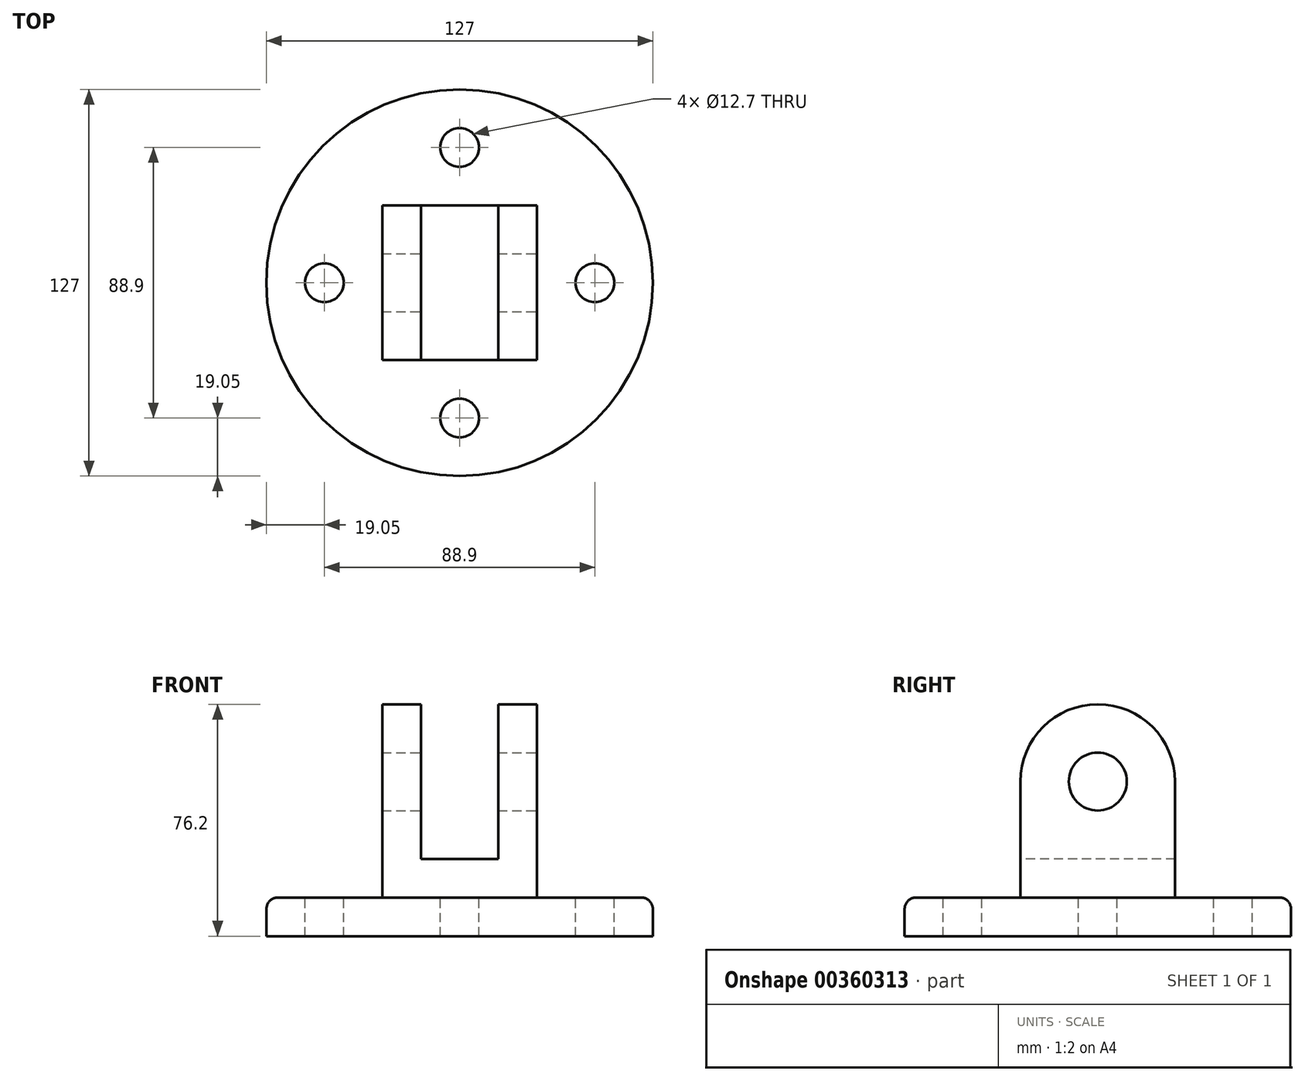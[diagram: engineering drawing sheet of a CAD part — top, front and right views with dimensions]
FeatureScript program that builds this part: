
annotation { "Feature Type Name" : "Feature", "Feature Type Description" : "" }
export const myFeature = defineFeature(function(context is Context, id is Id, definition is map)
    precondition{}
    {
        {
            var Q0;
            Q0=qCreatedBy(makeId("Top.planeOp"),FACE);
            var sketch = newSketch(context, id + "F0", { "sketchPlane" : qUnion([Q0])});
            skCircle(sketch, "E0", {"center": v(0, 0) * mm, "radius": 63.5 * mm});
            skSolve(sketch);
        }
        {
            var Q0;
            Q0 = qSketchRegion(id + "F0", true);
            extrude(context, id + "F1", {"entities" : qUnion([Q0]), "depth" : 12.7 * mm});
        }
        {
            var Q0;
            Q0=makeQuery(id+"F1.opExtrude","CAP_FACE",FACE,{"disambiguationData":[OSD([sQuery(id+"F0.wireOp",EDGE,"E0")])],"isStart":false});
            var sketch = newSketch(context, id + "F2", { "sketchPlane" : qUnion([Q0])});
            skLineSegment(sketch, "E1.bottom", {"start": v(25.4, 25.4) * mm, "end": v(-25.4, 25.4) * mm});
            skLineSegment(sketch, "E1.top", {"start": v(25.4, -25.4) * mm, "end": v(-25.4, -25.4) * mm});
            skLineSegment(sketch, "E1.left", {"start": v(25.4, 25.4) * mm, "end": v(25.4, -25.4) * mm});
            skLineSegment(sketch, "E1.right", {"start": v(-25.4, 25.4) * mm, "end": v(-25.4, -25.4) * mm});
            skPoint(sketch, "E1.middle", {"position": v(0, 0) * mm});
            skSolve(sketch);
        }
        {
            var Q0;
            Q0 = qSketchRegion(id + "F2", true);
            extrude(context, id + "F3", {"entities" : qUnion([Q0]), "operationType" : NewBodyOperationType.ADD, "depth" : 12.7 * mm});
        }
        {
            var Q0;
            Q0=makeQuery(id+"F3.opExtrude","CAP_FACE",FACE,{"disambiguationData":[OSD([sQuery(id+"F2.wireOp",EDGE,"E1.bottom"),sQuery(id+"F2.wireOp",EDGE,"E1.top"),sQuery(id+"F2.wireOp",EDGE,"E1.left"),sQuery(id+"F2.wireOp",EDGE,"E1.right")])],"isStart":false});
            var sketch = newSketch(context, id + "F4", { "sketchPlane" : qUnion([Q0])});
            skLineSegment(sketch, "E2.bottom", {"start": v(-10.67, -25.4) * mm, "end": v(-25.4, -25.4) * mm});
            skLineSegment(sketch, "E2.top", {"start": v(-10.67, 25.4) * mm, "end": v(-25.4, 25.4) * mm});
            skLineSegment(sketch, "E2.left", {"start": v(-10.67, -25.4) * mm, "end": v(-10.67, 25.4) * mm});
            skLineSegment(sketch, "E2.right", {"start": v(-25.4, -25.4) * mm, "end": v(-25.4, 25.4) * mm});
            skLineSegment(sketch, "E3.bottom", {"start": v(25.4, -25.4) * mm, "end": v(12.7, -25.4) * mm});
            skLineSegment(sketch, "E3.top", {"start": v(25.4, 25.4) * mm, "end": v(12.7, 25.4) * mm});
            skLineSegment(sketch, "E3.left", {"start": v(25.4, -25.4) * mm, "end": v(25.4, 25.4) * mm});
            skLineSegment(sketch, "E3.right", {"start": v(12.7, -25.4) * mm, "end": v(12.7, 25.4) * mm});
            skSolve(sketch);
        }
        {
            var Q0;
            Q0 = qSketchRegion(id + "F4", true);
            extrude(context, id + "F5", {"entities" : qUnion([Q0]), "operationType" : NewBodyOperationType.ADD, "depth" : 25.4 * mm});
        }
        {
            var Q0;
            Q0=qCreatedBy(makeId("Right.planeOp"),FACE);
            var sketch = newSketch(context, id + "F6", { "sketchPlane" : qUnion([Q0])});
            skArc(sketch, "E4", {"start": v(25.4, 50.8) * mm, "mid": v(0, 76.2) * mm, "end": v(-25.4, 50.8) * mm});
            skLineSegment(sketch, "E5", {"start": v(-25.4, 50.8) * mm, "end": v(25.4, 50.8) * mm});
            skSolve(sketch);
        }
        {
            var Q0;
            Q0 = qSketchRegion(id + "F6", true);
            extrude(context, id + "F7", {"entities" : qUnion([Q0]), "operationType" : NewBodyOperationType.ADD, "depth" : 25.4 * mm, "hasSecondDirection" : true, "secondDirectionOppositeDirection" : true, "secondDirectionDepth" : 25.4 * mm});
        }
        {
            var Q0;
            Q0=makeQuery(id+"F1.opExtrude","CAP_FACE",FACE,{"disambiguationData":[OSD([sQuery(id+"F0.wireOp",EDGE,"E0")])],"isStart":false});
            var sketch = newSketch(context, id + "F8", { "sketchPlane" : qUnion([Q0])});
            skLineSegment(sketch, "E6.bottom", {"start": v(12.7, 25.4) * mm, "end": v(-12.7, 25.4) * mm});
            skLineSegment(sketch, "E6.top", {"start": v(12.7, -25.4) * mm, "end": v(-12.7, -25.4) * mm});
            skLineSegment(sketch, "E6.left", {"start": v(12.7, 25.4) * mm, "end": v(12.7, -25.4) * mm});
            skLineSegment(sketch, "E6.right", {"start": v(-12.7, 25.4) * mm, "end": v(-12.7, -25.4) * mm});
            skPoint(sketch, "E6.middle", {"position": v(0, 0) * mm});
            skSolve(sketch);
        }
        {
            var Q0;
            Q0 = qSketchRegion(id + "F8", true);
            extrude(context, id + "F9", {"entities" : qUnion([Q0]), "operationType" : NewBodyOperationType.REMOVE, "depth" : 73.66 * mm});
        }
        {
            var Q0;
            Q0=makeQuery(id+"F9.boolean.opBoolean","MERGE",FACE,{"derivedFrom":[makeQuery(id+"F1.opExtrude","CAP_FACE",FACE,{"disambiguationData":[OSD([sQuery(id+"F0.wireOp",EDGE,"E0")])],"isStart":false}),makeQuery(id+"F9.opExtrude","CAP_FACE",FACE,{"disambiguationData":[OSD([sQuery(id+"F8.wireOp",EDGE,"E6.bottom"),sQuery(id+"F8.wireOp",EDGE,"E6.top"),sQuery(id+"F8.wireOp",EDGE,"E6.left"),sQuery(id+"F8.wireOp",EDGE,"E6.right")])],"isStart":true})]});
            var sketch = newSketch(context, id + "F10", { "sketchPlane" : qUnion([Q0])});
            skLineSegment(sketch, "E7.bottom", {"start": v(12.7, 25.4) * mm, "end": v(-12.7, 25.4) * mm});
            skLineSegment(sketch, "E7.top", {"start": v(12.7, -25.4) * mm, "end": v(-12.7, -25.4) * mm});
            skLineSegment(sketch, "E7.left", {"start": v(12.7, 25.4) * mm, "end": v(12.7, -25.4) * mm});
            skLineSegment(sketch, "E7.right", {"start": v(-12.7, 25.4) * mm, "end": v(-12.7, -25.4) * mm});
            skPoint(sketch, "E7.middle", {"position": v(0, 0) * mm});
            skSolve(sketch);
        }
        {
            var Q0;
            Q0 = qSketchRegion(id + "F10", true);
            extrude(context, id + "F11", {"entities" : qUnion([Q0]), "operationType" : NewBodyOperationType.ADD, "depth" : 12.7 * mm});
        }
        {
            var Q0;
            Q0=qCreatedBy(makeId("Right.planeOp"),FACE);
            var sketch = newSketch(context, id + "F12", { "sketchPlane" : qUnion([Q0])});
            skCircle(sketch, "E8", {"center": v(0, 50.8) * mm, "radius": 9.53 * mm});
            skSolve(sketch);
        }
        {
            var Q0;
            Q0 = qSketchRegion(id + "F12", true);
            extrude(context, id + "F13", {"entities" : qUnion([Q0]), "operationType" : NewBodyOperationType.REMOVE, "endBound" : BoundingType.THROUGH_ALL, "oppositeDirection" : true, "depth" : 25.4 * mm, "hasSecondDirection" : true, "secondDirectionOppositeDirection" : false, "secondDirectionDepth" : 43.69 * mm});
        }
        {
            var Q0;
            Q0=makeQuery(id+"F9.boolean.opBoolean","MERGE",FACE,{"derivedFrom":[makeQuery(id+"F1.opExtrude","CAP_FACE",FACE,{"disambiguationData":[OSD([sQuery(id+"F0.wireOp",EDGE,"E0")])],"isStart":false}),makeQuery(id+"F9.opExtrude","CAP_FACE",FACE,{"disambiguationData":[OSD([sQuery(id+"F8.wireOp",EDGE,"E6.bottom"),sQuery(id+"F8.wireOp",EDGE,"E6.top"),sQuery(id+"F8.wireOp",EDGE,"E6.left"),sQuery(id+"F8.wireOp",EDGE,"E6.right")])],"isStart":true})]});
            var sketch = newSketch(context, id + "F14", { "sketchPlane" : qUnion([Q0])});
            skCircle(sketch, "E9", {"center": v(0, 0) * mm, "radius": 44.45 * mm, "construction": true});
            skCircle(sketch, "E10", {"center": v(44.45, 0) * mm, "radius": 6.35 * mm});
            skCircle(sketch, "E11", {"center": v(0, 44.45) * mm, "radius": 6.35 * mm});
            skCircle(sketch, "E12", {"center": v(-44.45, 0) * mm, "radius": 6.35 * mm});
            skCircle(sketch, "E13", {"center": v(0, -44.45) * mm, "radius": 6.35 * mm});
            skSolve(sketch);
        }
        {
            var Q0;
            Q0 = qSketchRegion(id + "F14", true);
            extrude(context, id + "F15", {"entities" : qUnion([Q0]), "operationType" : NewBodyOperationType.REMOVE, "endBound" : BoundingType.THROUGH_ALL, "oppositeDirection" : true, "depth" : 25.4 * mm});
        }
        {
            var Q0;
            {var subQ4=sQuery(id+"F2.wireOp",EDGE,"E1.top");var subQ10=makeQuery(id+"F3.opExtrude","CAP_EDGE",EDGE,{"disambiguationData":[OSD([subQ4])],"isStart":true});Q0=makeQuery(id+"F11.boolean.opBoolean","MERGE",EDGE,{"derivedFrom":[makeQuery(id+"F9.boolean.opBoolean","SPLIT",EDGE,{"disambiguationData":[TD([makeQuery(id+"F3.opExtrude","SWEPT_FACE",FACE,{"disambiguationData":[OSD([sQuery(id+"F2.wireOp",EDGE,"E1.left")])]})])],"derivedFrom":subQ10}),makeQuery(id+"F9.boolean.opBoolean","SPLIT",EDGE,{"disambiguationData":[TD([makeQuery(id+"F3.opExtrude","SWEPT_FACE",FACE,{"disambiguationData":[OSD([sQuery(id+"F2.wireOp",EDGE,"E1.right")])]})])],"derivedFrom":subQ10}),makeQuery(id+"F11.opExtrude","CAP_EDGE",EDGE,{"disambiguationData":[OSD([sQuery(id+"F10.wireOp",EDGE,"E7.top")])],"isStart":true})]});}
            var Q1;
            Q1=makeQuery(id+"F3.opExtrude","CAP_EDGE",EDGE,{"disambiguationData":[OSD([sQuery(id+"F2.wireOp",EDGE,"E1.left")])],"isStart":true});
            var Q2;
            {var subQ4=sQuery(id+"F2.wireOp",EDGE,"E1.bottom");var subQ10=makeQuery(id+"F3.opExtrude","CAP_EDGE",EDGE,{"disambiguationData":[OSD([subQ4])],"isStart":true});Q2=makeQuery(id+"F11.boolean.opBoolean","MERGE",EDGE,{"derivedFrom":[makeQuery(id+"F9.boolean.opBoolean","SPLIT",EDGE,{"disambiguationData":[TD([makeQuery(id+"F3.opExtrude","SWEPT_FACE",FACE,{"disambiguationData":[OSD([sQuery(id+"F2.wireOp",EDGE,"E1.left")])]})])],"derivedFrom":subQ10}),makeQuery(id+"F9.boolean.opBoolean","SPLIT",EDGE,{"disambiguationData":[TD([makeQuery(id+"F3.opExtrude","SWEPT_FACE",FACE,{"disambiguationData":[OSD([sQuery(id+"F2.wireOp",EDGE,"E1.right")])]})])],"derivedFrom":subQ10}),makeQuery(id+"F11.opExtrude","CAP_EDGE",EDGE,{"disambiguationData":[OSD([sQuery(id+"F10.wireOp",EDGE,"E7.bottom")])],"isStart":true})]});}
            var Q3;
            Q3=makeQuery(id+"F3.opExtrude","CAP_EDGE",EDGE,{"disambiguationData":[OSD([sQuery(id+"F2.wireOp",EDGE,"E1.right")])],"isStart":true});
            var Q4;
            Q4=makeQuery(id+"F1.opExtrude","CAP_EDGE",EDGE,{"disambiguationData":[OSD([sQuery(id+"F0.wireOp",EDGE,"E0")])],"isStart":false});
            fillet(context, id + "F16", {"entities" : qUnion([Q0, Q1, Q2, Q3, Q4]), "radius" : 3.8 * mm, "tangentPropagation" : true, "allowEdgeOverflow" : false});
        }
    });
